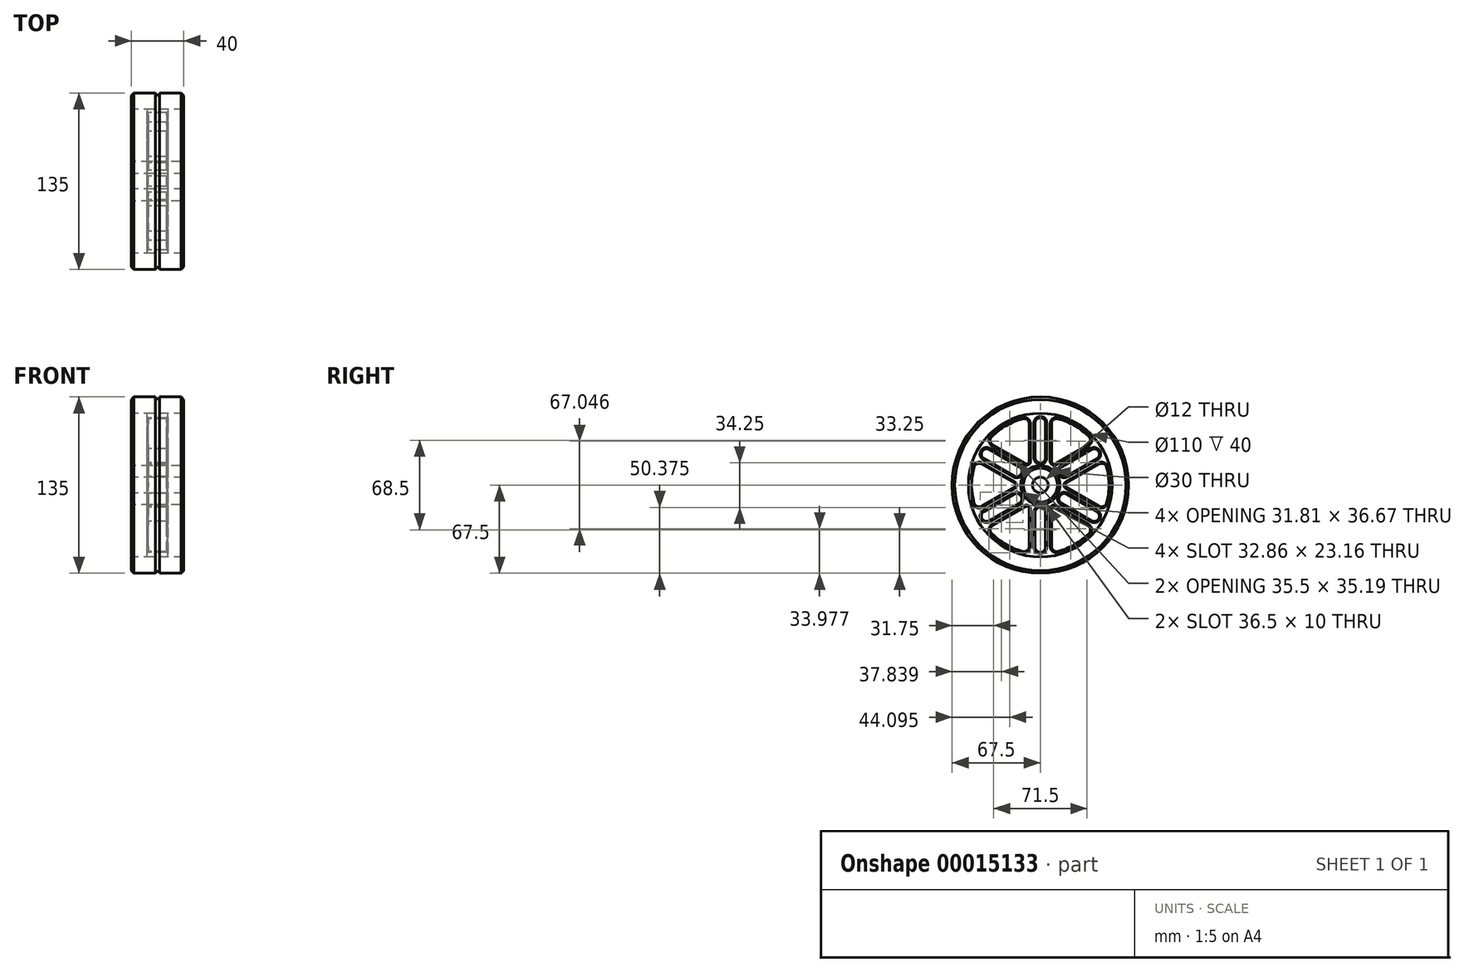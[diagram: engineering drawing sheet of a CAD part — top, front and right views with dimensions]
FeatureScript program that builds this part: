
annotation { "Feature Type Name" : "Feature", "Feature Type Description" : "" }
export const myFeature = defineFeature(function(context is Context, id is Id, definition is map)
    precondition{}
    {
        {
            var Q0;
            Q0=qCreatedBy(makeId("Right.planeOp"),FACE);
            var sketch = newSketch(context, id + "F0", { "sketchPlane" : qUnion([Q0])});
            skCircle(sketch, "E0", {"center": v(0, 0) * mm, "radius": 6 * mm});
            skCircle(sketch, "E1", {"center": v(0, 0) * mm, "radius": 15 * mm});
            skCircle(sketch, "E2", {"center": v(0, 0) * mm, "radius": 55 * mm});
            skCircle(sketch, "E3", {"center": v(0, 0) * mm, "radius": 67.5 * mm});
            skLineSegment(sketch, "E4", {"start": v(0, 0) * mm, "end": v(0, 73.7) * mm, "construction": true});
            skCircle(sketch, "E5", {"center": v(0, 0) * mm, "radius": 47.5 * mm, "construction": true});
            skCircle(sketch, "E6", {"center": v(0, 0) * mm, "radius": 21 * mm, "construction": true});
            skArc(sketch, "E7", {"start": v(-4, 21) * mm, "mid": v(0, 17) * mm, "end": v(4, 21) * mm});
            skArc(sketch, "E8", {"start": v(4, 47.33) * mm, "mid": v(0, 51.5) * mm, "end": v(-4, 47.33) * mm});
            skLineSegment(sketch, "E9", {"start": v(-4, 47.5) * mm, "end": v(-4, 20.62) * mm});
            skLineSegment(sketch, "E10", {"start": v(4, 47.5) * mm, "end": v(4, 20.62) * mm});
            skLineSegment(sketch, "E11.1.0", {"start": v(-43.14, 20.29) * mm, "end": v(-19.85, 6.84) * mm});
            skLineSegment(sketch, "E11.1.1", {"start": v(-39.14, 27.21) * mm, "end": v(-15.85, 13.77) * mm});
            skArc(sketch, "E11.1.2", {"start": v(-39, 27.13) * mm, "mid": v(-44.6, 25.75) * mm, "end": v(-42.99, 20.2) * mm});
            skArc(sketch, "E11.1.3", {"start": v(-20.19, 7.04) * mm, "mid": v(-14.72, 8.5) * mm, "end": v(-16.19, 13.96) * mm});
            skLineSegment(sketch, "E11.2.0", {"start": v(-39.14, -27.21) * mm, "end": v(-15.85, -13.77) * mm});
            skLineSegment(sketch, "E11.2.1", {"start": v(-43.14, -20.29) * mm, "end": v(-19.85, -6.84) * mm});
            skArc(sketch, "E11.2.2", {"start": v(-42.99, -20.2) * mm, "mid": v(-44.6, -25.75) * mm, "end": v(-39, -27.13) * mm});
            skArc(sketch, "E11.2.3", {"start": v(-16.19, -13.96) * mm, "mid": v(-14.72, -8.5) * mm, "end": v(-20.19, -7.04) * mm});
            skLineSegment(sketch, "E12.2.3.0", {"start": v(4, -47.5) * mm, "end": v(4, -20.62) * mm});
            skLineSegment(sketch, "E12.3.3.0", {"start": v(-4, -47.5) * mm, "end": v(-4, -20.62) * mm});
            skArc(sketch, "E12.6.3.0", {"start": v(-4, -47.33) * mm, "mid": v(0, -51.5) * mm, "end": v(4, -47.33) * mm});
            skArc(sketch, "E12.10.3.0", {"start": v(4, -21) * mm, "mid": v(0, -17) * mm, "end": v(-4, -21) * mm});
            skLineSegment(sketch, "E12.2.4.0", {"start": v(43.14, -20.29) * mm, "end": v(19.85, -6.84) * mm});
            skLineSegment(sketch, "E12.3.4.0", {"start": v(39.14, -27.21) * mm, "end": v(15.85, -13.77) * mm});
            skArc(sketch, "E12.6.4.0", {"start": v(39, -27.13) * mm, "mid": v(44.6, -25.75) * mm, "end": v(42.99, -20.2) * mm});
            skArc(sketch, "E12.10.4.0", {"start": v(20.19, -7.04) * mm, "mid": v(14.72, -8.5) * mm, "end": v(16.19, -13.96) * mm});
            skLineSegment(sketch, "E12.2.5.0", {"start": v(39.14, 27.21) * mm, "end": v(15.85, 13.77) * mm});
            skLineSegment(sketch, "E12.3.5.0", {"start": v(43.14, 20.29) * mm, "end": v(19.85, 6.84) * mm});
            skArc(sketch, "E12.6.5.0", {"start": v(42.99, 20.2) * mm, "mid": v(44.6, 25.75) * mm, "end": v(39, 27.13) * mm});
            skArc(sketch, "E12.10.5.0", {"start": v(16.19, 13.96) * mm, "mid": v(14.72, 8.5) * mm, "end": v(20.19, 7.04) * mm});
            skLineSegment(sketch, "E13.0", {"start": v(-8.5, 46.86) * mm, "end": v(-8.5, 18.19) * mm});
            skLineSegment(sketch, "E14.0", {"start": v(-36.33, 30.8) * mm, "end": v(-11.5, 16.45) * mm});
            skArc(sketch, "E15", {"start": v(-40.62, 33.26) * mm, "mid": v(26.25, -45.47) * mm, "end": v(-8.5, 51.8) * mm, "construction": true});
            skArc(sketch, "E16", {"start": v(-13.53, 50.73) * mm, "mid": v(-26.25, 45.47) * mm, "end": v(-37.16, 37.08) * mm});
            skPoint(sketch, "E17.visualSharp", {"position": v(-8.5, 14.72) * mm});
            skArc(sketch, "E17.filletArc", {"start": v(-11.5, 16.45) * mm, "mid": v(-9.5, 16.45) * mm, "end": v(-8.5, 18.19) * mm});
            skPoint(sketch, "E18.visualSharp", {"position": v(-40.62, 33.26) * mm});
            skArc(sketch, "E18.filletArc", {"start": v(-37.16, 37.08) * mm, "mid": v(-38.3, 33.73) * mm, "end": v(-36.33, 30.8) * mm});
            skPoint(sketch, "E19.visualSharp", {"position": v(-8.5, 51.8) * mm});
            skArc(sketch, "E19.filletArc", {"start": v(-8.5, 46.86) * mm, "mid": v(-10.06, 50.03) * mm, "end": v(-13.53, 50.73) * mm});
            skLineSegment(sketch, "E20.1.0", {"start": v(-44.83, -16.07) * mm, "end": v(-20, -1.73) * mm});
            skArc(sketch, "E20.1.1", {"start": v(-50.7, -13.65) * mm, "mid": v(-48.36, -16.3) * mm, "end": v(-44.83, -16.07) * mm});
            skArc(sketch, "E20.1.2", {"start": v(-50.7, 13.65) * mm, "mid": v(-52.5, 0) * mm, "end": v(-50.7, -13.65) * mm});
            skArc(sketch, "E20.1.3", {"start": v(-44.83, 16.07) * mm, "mid": v(-48.36, 16.3) * mm, "end": v(-50.7, 13.65) * mm});
            skLineSegment(sketch, "E20.1.4", {"start": v(-44.83, 16.07) * mm, "end": v(-20, 1.73) * mm});
            skArc(sketch, "E20.1.5", {"start": v(-20, -1.73) * mm, "mid": v(-19, 0) * mm, "end": v(-20, 1.73) * mm});
            skLineSegment(sketch, "E20.2.0", {"start": v(-8.5, -46.86) * mm, "end": v(-8.5, -18.19) * mm});
            skArc(sketch, "E20.2.1", {"start": v(-13.53, -50.73) * mm, "mid": v(-10.06, -50.03) * mm, "end": v(-8.5, -46.86) * mm});
            skArc(sketch, "E20.2.2", {"start": v(-37.16, -37.08) * mm, "mid": v(-26.25, -45.47) * mm, "end": v(-13.53, -50.73) * mm});
            skArc(sketch, "E20.2.3", {"start": v(-36.33, -30.8) * mm, "mid": v(-38.3, -33.73) * mm, "end": v(-37.16, -37.08) * mm});
            skLineSegment(sketch, "E20.2.4", {"start": v(-36.33, -30.8) * mm, "end": v(-11.5, -16.45) * mm});
            skArc(sketch, "E20.2.5", {"start": v(-8.5, -18.19) * mm, "mid": v(-9.5, -16.45) * mm, "end": v(-11.5, -16.45) * mm});
            skLineSegment(sketch, "E20.3.0", {"start": v(36.33, -30.8) * mm, "end": v(11.5, -16.45) * mm});
            skArc(sketch, "E20.3.1", {"start": v(37.16, -37.08) * mm, "mid": v(38.3, -33.73) * mm, "end": v(36.33, -30.8) * mm});
            skArc(sketch, "E20.3.2", {"start": v(13.53, -50.73) * mm, "mid": v(26.25, -45.47) * mm, "end": v(37.16, -37.08) * mm});
            skArc(sketch, "E20.3.3", {"start": v(8.5, -46.86) * mm, "mid": v(10.06, -50.03) * mm, "end": v(13.53, -50.73) * mm});
            skLineSegment(sketch, "E20.3.4", {"start": v(8.5, -46.86) * mm, "end": v(8.5, -18.19) * mm});
            skArc(sketch, "E20.3.5", {"start": v(11.5, -16.45) * mm, "mid": v(9.5, -16.45) * mm, "end": v(8.5, -18.19) * mm});
            skLineSegment(sketch, "E20.4.0", {"start": v(44.83, 16.07) * mm, "end": v(20, 1.73) * mm});
            skArc(sketch, "E20.4.1", {"start": v(50.7, 13.65) * mm, "mid": v(48.36, 16.3) * mm, "end": v(44.83, 16.07) * mm});
            skArc(sketch, "E20.4.2", {"start": v(50.7, -13.65) * mm, "mid": v(52.5, 0) * mm, "end": v(50.7, 13.65) * mm});
            skArc(sketch, "E20.4.3", {"start": v(44.83, -16.07) * mm, "mid": v(48.36, -16.3) * mm, "end": v(50.7, -13.65) * mm});
            skLineSegment(sketch, "E20.4.4", {"start": v(44.83, -16.07) * mm, "end": v(20, -1.73) * mm});
            skArc(sketch, "E20.4.5", {"start": v(20, 1.73) * mm, "mid": v(19, 0) * mm, "end": v(20, -1.73) * mm});
            skLineSegment(sketch, "E20.5.0", {"start": v(8.5, 46.86) * mm, "end": v(8.5, 18.19) * mm});
            skArc(sketch, "E20.5.1", {"start": v(13.53, 50.73) * mm, "mid": v(10.06, 50.03) * mm, "end": v(8.5, 46.86) * mm});
            skArc(sketch, "E20.5.2", {"start": v(37.16, 37.08) * mm, "mid": v(26.25, 45.47) * mm, "end": v(13.53, 50.73) * mm});
            skArc(sketch, "E20.5.3", {"start": v(36.33, 30.8) * mm, "mid": v(38.3, 33.73) * mm, "end": v(37.16, 37.08) * mm});
            skLineSegment(sketch, "E20.5.4", {"start": v(36.33, 30.8) * mm, "end": v(11.5, 16.45) * mm});
            skArc(sketch, "E20.5.5", {"start": v(8.5, 18.19) * mm, "mid": v(9.5, 16.45) * mm, "end": v(11.5, 16.45) * mm});
            skSolve(sketch);
        }
        {
            var Q0;
            Q0=makeQuery(id+"F0.imprint","IMPRINT",FACE,{"disambiguationData":[TD([[makeQuery(id+"F0.imprint","IMPRINT",EDGE,{"derivedFrom":sQuery(id+"F0.wireOp",EDGE,"E1")}),-1.0]])]});
            extrude(context, id + "F1", {"entities" : qUnion([Q0]), "endBound" : BoundingType.SYMMETRIC, "depth" : 16 * mm});
        }
        {
            var Q0;
            Q0=makeQuery(id+"F0.imprint","IMPRINT",FACE,{"disambiguationData":[TD([[makeQuery(id+"F0.imprint","IMPRINT",EDGE,{"derivedFrom":sQuery(id+"F0.wireOp",EDGE,"E2")}),-1.0]])]});
            var Q1;
            Q1=makeQuery(id+"F0.imprint","IMPRINT",FACE,{"disambiguationData":[TD([[makeQuery(id+"F0.imprint","IMPRINT",EDGE,{"derivedFrom":sQuery(id+"F0.wireOp",EDGE,"E0")}),-1.0]])]});
            extrude(context, id + "F2", {"entities" : qUnion([Q0, Q1]), "endBound" : BoundingType.SYMMETRIC, "depth" : 40 * mm});
        }
        {
            var Q0;
            Q0=qCreatedBy(makeId("Front.planeOp"),FACE);
            var sketch = newSketch(context, id + "F3", { "sketchPlane" : qUnion([Q0])});
            skLineSegment(sketch, "E21", {"start": v(-20, 67.5) * mm, "end": v(20, 67.5) * mm});
            skLineSegment(sketch, "E22", {"start": v(20, -67.5) * mm, "end": v(-20, -67.5) * mm});
            skCircle(sketch, "E23", {"center": v(0, 67.5) * mm, "radius": 1.5 * mm});
            skSolve(sketch);
        }
        {
            var Q0;
            {var subQ0=sQuery(id+"F3.wireOp",EDGE,"E23");var subQ1=sQuery(id+"F3.wireOp",EDGE,"E21");var subQ3=makeQuery(id+"F3.imprint","INTERSECT",VERTEX,{"disambiguationData":[OD(0.0)],"derivedFrom":[subQ1,subQ0]});Q0=makeQuery(id+"F3.imprint","IMPRINT",FACE,{"disambiguationData":[TD([[makeQuery(id+"F3.imprint","IMPRINT",EDGE,{"disambiguationData":[TD([[subQ3,-1.0]])],"derivedFrom":subQ1}),-1.0]])]});}
            var Q1;
            {var subQ0=sQuery(id+"F3.wireOp",EDGE,"E23");var subQ1=sQuery(id+"F3.wireOp",EDGE,"E21");var subQ3=makeQuery(id+"F3.imprint","INTERSECT",VERTEX,{"disambiguationData":[OD(0.0)],"derivedFrom":[subQ1,subQ0]});Q1=makeQuery(id+"F3.imprint","IMPRINT",FACE,{"disambiguationData":[TD([[makeQuery(id+"F3.imprint","IMPRINT",EDGE,{"disambiguationData":[TD([[subQ3,-1.0]])],"derivedFrom":subQ1}),1.0]])]});}
            var Q2;
            Q2=makeQuery(id+"F2.opExtrude","SWEPT_FACE",FACE,{"disambiguationData":[OSD([sQuery(id+"F0.wireOp",EDGE,"E1")])]});
            revolve(context, id + "F4", {"operationType" : NewBodyOperationType.REMOVE, "entities" : qUnion([Q0, Q1]), "axis" : qUnion([Q2]), "revolveType" : RevolveType.FULL, "oppositeDirection" : true});
        }
        {
            var Q0;
            Q0=makeQuery(id+"F2.opExtrude","CAP_EDGE",EDGE,{"disambiguationData":[OSD([sQuery(id+"F0.wireOp",EDGE,"E3")])],"isStart":false});
            var Q1;
            Q1=makeQuery(id+"F2.opExtrude","CAP_EDGE",EDGE,{"disambiguationData":[OSD([sQuery(id+"F0.wireOp",EDGE,"E3")])],"isStart":true});
            var Q2;
            Q2=makeQuery(id+"F2.opExtrude","CAP_EDGE",EDGE,{"disambiguationData":[OSD([sQuery(id+"F0.wireOp",EDGE,"E1")])],"isStart":false});
            var Q3;
            Q3=makeQuery(id+"F2.opExtrude","CAP_EDGE",EDGE,{"disambiguationData":[OSD([sQuery(id+"F0.wireOp",EDGE,"E1")])],"isStart":true});
            chamfer(context, id + "F5", {"entities" : qUnion([Q0, Q1, Q2, Q3]), "width" : 2 * mm, "tangentPropagation" : true});
        }
        {
            var Q0;
            Q0=makeQuery(id+"F1.opExtrude","CAP_EDGE",EDGE,{"disambiguationData":[OSD([sQuery(id+"F0.wireOp",EDGE,"E14.0")])],"isStart":false});
            var Q1;
            Q1=makeQuery(id+"F1.opExtrude","CAP_EDGE",EDGE,{"disambiguationData":[OSD([sQuery(id+"F0.wireOp",EDGE,"E9")])],"isStart":false});
            var Q2;
            Q2=makeQuery(id+"F1.opExtrude","CAP_EDGE",EDGE,{"disambiguationData":[OSD([sQuery(id+"F0.wireOp",EDGE,"E20.5.0")])],"isStart":false});
            var Q3;
            Q3=makeQuery(id+"F1.opExtrude","CAP_EDGE",EDGE,{"disambiguationData":[OSD([sQuery(id+"F0.wireOp",EDGE,"E12.2.5.0")])],"isStart":false});
            var Q4;
            Q4=makeQuery(id+"F1.opExtrude","CAP_EDGE",EDGE,{"disambiguationData":[OSD([sQuery(id+"F0.wireOp",EDGE,"E20.4.0")])],"isStart":false});
            var Q5;
            Q5=makeQuery(id+"F1.opExtrude","CAP_EDGE",EDGE,{"disambiguationData":[OSD([sQuery(id+"F0.wireOp",EDGE,"E12.2.4.0")])],"isStart":false});
            var Q6;
            Q6=makeQuery(id+"F1.opExtrude","CAP_EDGE",EDGE,{"disambiguationData":[OSD([sQuery(id+"F0.wireOp",EDGE,"E20.3.0")])],"isStart":false});
            var Q7;
            Q7=makeQuery(id+"F1.opExtrude","CAP_EDGE",EDGE,{"disambiguationData":[OSD([sQuery(id+"F0.wireOp",EDGE,"E12.3.3.0")])],"isStart":false});
            var Q8;
            Q8=makeQuery(id+"F1.opExtrude","CAP_EDGE",EDGE,{"disambiguationData":[OSD([sQuery(id+"F0.wireOp",EDGE,"E20.2.0")])],"isStart":false});
            var Q9;
            Q9=makeQuery(id+"F1.opExtrude","CAP_EDGE",EDGE,{"disambiguationData":[OSD([sQuery(id+"F0.wireOp",EDGE,"E11.2.0")])],"isStart":false});
            var Q10;
            Q10=makeQuery(id+"F1.opExtrude","CAP_EDGE",EDGE,{"disambiguationData":[OSD([sQuery(id+"F0.wireOp",EDGE,"E20.1.0")])],"isStart":false});
            var Q11;
            Q11=makeQuery(id+"F1.opExtrude","CAP_EDGE",EDGE,{"disambiguationData":[OSD([sQuery(id+"F0.wireOp",EDGE,"E11.1.0")])],"isStart":false});
            var Q12;
            Q12=makeQuery(id+"F1.opExtrude","CAP_EDGE",EDGE,{"disambiguationData":[OSD([sQuery(id+"F0.wireOp",EDGE,"E16")])],"isStart":true});
            var Q13;
            Q13=makeQuery(id+"F1.opExtrude","CAP_EDGE",EDGE,{"disambiguationData":[OSD([sQuery(id+"F0.wireOp",EDGE,"E11.1.2")])],"isStart":true});
            var Q14;
            Q14=makeQuery(id+"F1.opExtrude","CAP_EDGE",EDGE,{"disambiguationData":[OSD([sQuery(id+"F0.wireOp",EDGE,"E20.1.2")])],"isStart":true});
            var Q15;
            Q15=makeQuery(id+"F1.opExtrude","CAP_EDGE",EDGE,{"disambiguationData":[OSD([sQuery(id+"F0.wireOp",EDGE,"E11.2.2")])],"isStart":true});
            var Q16;
            Q16=makeQuery(id+"F1.opExtrude","CAP_EDGE",EDGE,{"disambiguationData":[OSD([sQuery(id+"F0.wireOp",EDGE,"E20.2.2")])],"isStart":true});
            var Q17;
            Q17=makeQuery(id+"F1.opExtrude","CAP_EDGE",EDGE,{"disambiguationData":[OSD([sQuery(id+"F0.wireOp",EDGE,"E12.10.3.0")])],"isStart":true});
            var Q18;
            Q18=makeQuery(id+"F1.opExtrude","CAP_EDGE",EDGE,{"disambiguationData":[OSD([sQuery(id+"F0.wireOp",EDGE,"E20.3.4")])],"isStart":true});
            var Q19;
            Q19=makeQuery(id+"F1.opExtrude","CAP_EDGE",EDGE,{"disambiguationData":[OSD([sQuery(id+"F0.wireOp",EDGE,"E12.10.4.0")])],"isStart":true});
            var Q20;
            Q20=makeQuery(id+"F1.opExtrude","CAP_EDGE",EDGE,{"disambiguationData":[OSD([sQuery(id+"F0.wireOp",EDGE,"E20.4.4")])],"isStart":true});
            var Q21;
            Q21=makeQuery(id+"F1.opExtrude","CAP_EDGE",EDGE,{"disambiguationData":[OSD([sQuery(id+"F0.wireOp",EDGE,"E12.10.5.0")])],"isStart":true});
            var Q22;
            Q22=makeQuery(id+"F1.opExtrude","CAP_EDGE",EDGE,{"disambiguationData":[OSD([sQuery(id+"F0.wireOp",EDGE,"E20.5.0")])],"isStart":true});
            var Q23;
            Q23=makeQuery(id+"F1.opExtrude","CAP_EDGE",EDGE,{"disambiguationData":[OSD([sQuery(id+"F0.wireOp",EDGE,"E10")])],"isStart":true});
            chamfer(context, id + "F6", {"entities" : qUnion([Q0, Q1, Q2, Q3, Q4, Q5, Q6, Q7, Q8, Q9, Q10, Q11, Q12, Q13, Q14, Q15, Q16, Q17, Q18, Q19, Q20, Q21, Q22, Q23]), "width" : 1 * mm, "tangentPropagation" : true});
        }
    });
